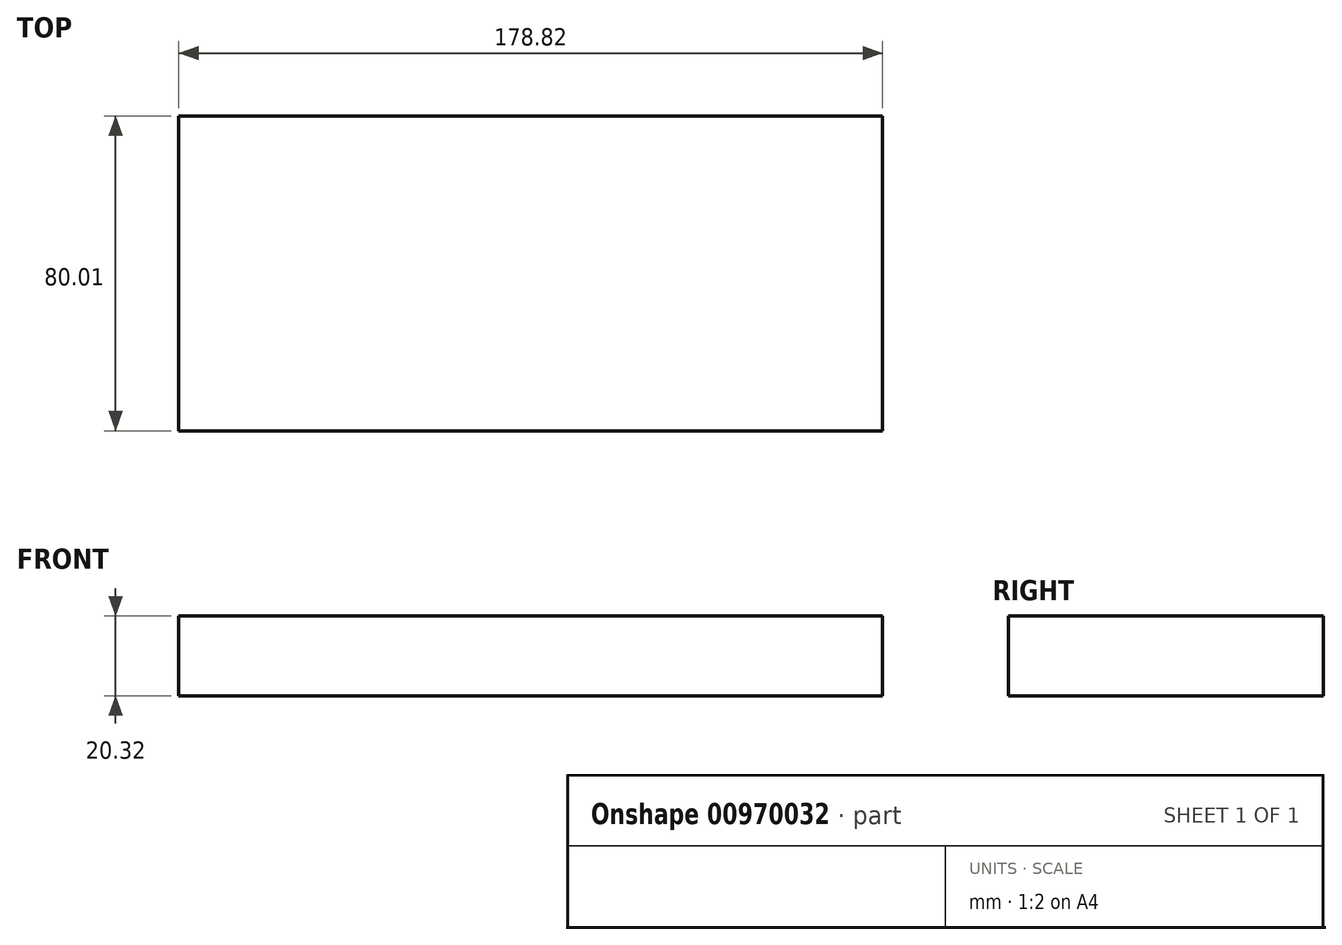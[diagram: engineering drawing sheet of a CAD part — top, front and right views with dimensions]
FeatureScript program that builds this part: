
annotation { "Feature Type Name" : "Feature", "Feature Type Description" : "" }
export const myFeature = defineFeature(function(context is Context, id is Id, definition is map)
    precondition{}
    {
        {
            var Q0;
            Q0=qCreatedBy(makeId("Top.planeOp"),FACE);
            var sketch = newSketch(context, id + "F0", { "sketchPlane" : qUnion([Q0])});
            skLineSegment(sketch, "E0.bottom", {"start": v(0, 0) * mm, "end": v(178.82, 0) * mm});
            skLineSegment(sketch, "E0.top", {"start": v(0, 80.01) * mm, "end": v(178.82, 80.01) * mm});
            skLineSegment(sketch, "E0.left", {"start": v(0, 0) * mm, "end": v(0, 80.01) * mm});
            skLineSegment(sketch, "E0.right", {"start": v(178.82, 0) * mm, "end": v(178.82, 80.01) * mm});
            skSolve(sketch);
        }
        {
            var Q0;
            Q0=makeQuery(id+"F0.imprint","IMPRINT",FACE,{"disambiguationData":[TD([[makeQuery(id+"F0.imprint","IMPRINT",EDGE,{"derivedFrom":sQuery(id+"F0.wireOp",EDGE,"E0.bottom")}),1.0]])]});
            extrude(context, id + "F1", {"entities" : qUnion([Q0]), "depth" : 20.32 * mm, "offsetDistance" : 25.4 * mm});
        }
    });
